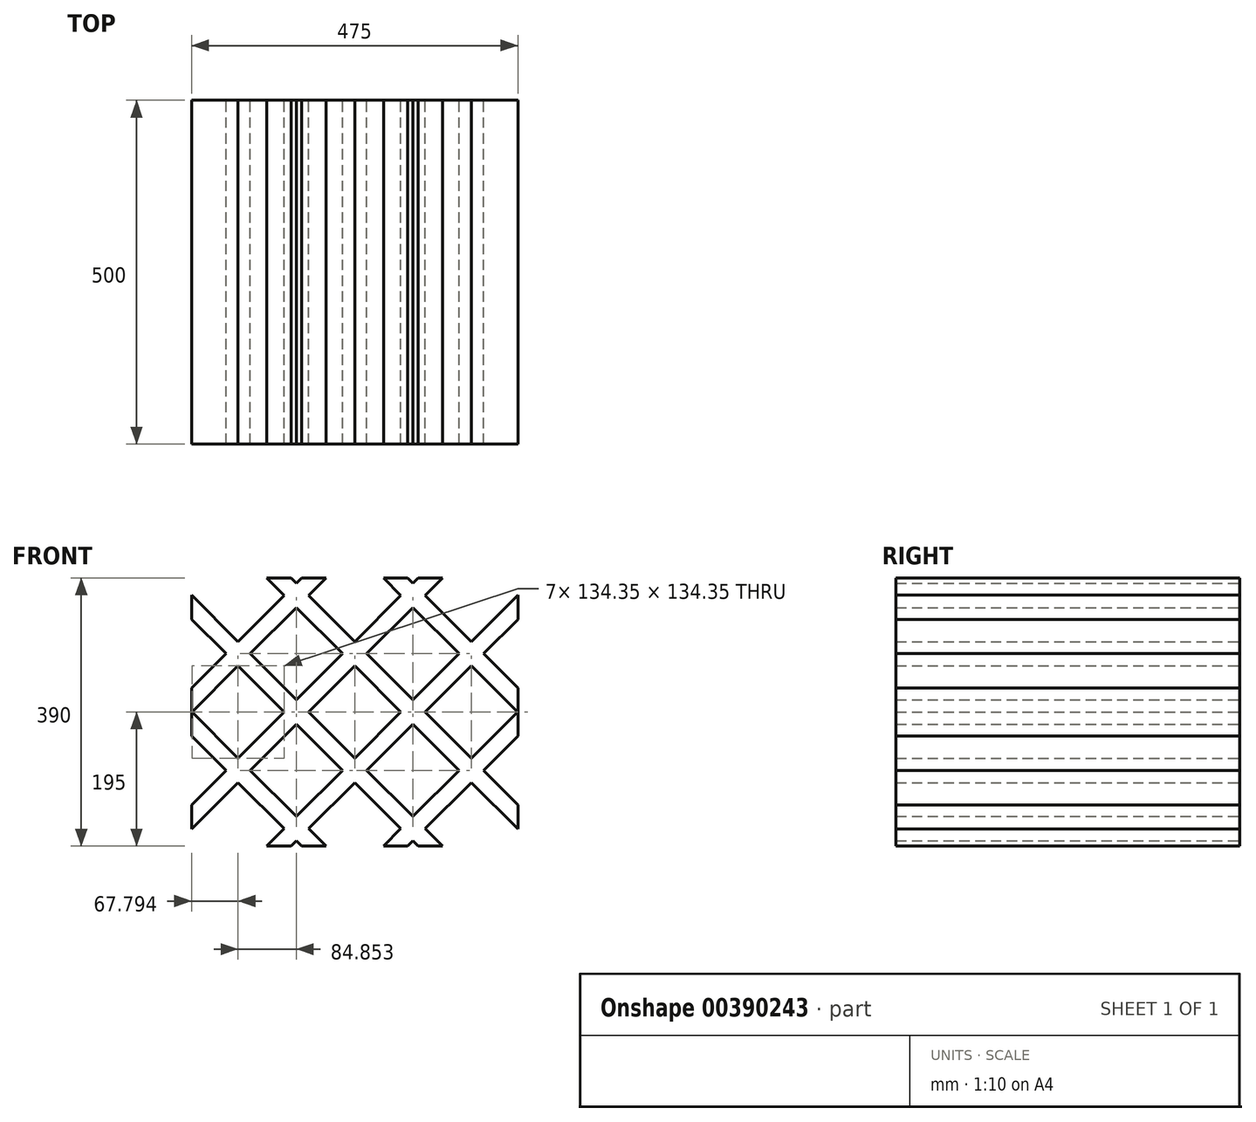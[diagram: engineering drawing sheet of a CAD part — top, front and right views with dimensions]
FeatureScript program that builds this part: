
annotation { "Feature Type Name" : "Feature", "Feature Type Description" : "" }
export const myFeature = defineFeature(function(context is Context, id is Id, definition is map)
    precondition{}
    {
        {
            var Q0;
            Q0=qCreatedBy(makeId("Front.planeOp"),FACE);
            var sketch = newSketch(context, id + "F0", { "sketchPlane" : qUnion([Q0])});
            skLineSegment(sketch, "E0.bottom", {"start": v(237.5, -195) * mm, "end": v(-237.5, -195) * mm, "construction": true});
            skLineSegment(sketch, "E0.top", {"start": v(237.5, 195) * mm, "end": v(-237.5, 195) * mm, "construction": true});
            skLineSegment(sketch, "E0.left", {"start": v(237.5, -195) * mm, "end": v(237.5, 195) * mm, "construction": true});
            skLineSegment(sketch, "E0.right", {"start": v(-237.5, -195) * mm, "end": v(-237.5, 195) * mm, "construction": true});
            skPoint(sketch, "E0.middle", {"position": v(0, 0) * mm});
            skLineSegment(sketch, "E1", {"start": v(-237.5, 152.65) * mm, "end": v(110.15, -195) * mm, "construction": true});
            skLineSegment(sketch, "E2", {"start": v(-110.15, 195) * mm, "end": v(237.5, -152.65) * mm, "construction": true});
            skLineSegment(sketch, "E3", {"start": v(59.56, 195) * mm, "end": v(237.5, 17.06) * mm, "construction": true});
            skLineSegment(sketch, "E4", {"start": v(-237.5, -17.06) * mm, "end": v(-59.56, -195) * mm, "construction": true});
            skLineSegment(sketch, "E5", {"start": v(110.15, 195) * mm, "end": v(-237.5, -152.65) * mm, "construction": true});
            skLineSegment(sketch, "E6", {"start": v(237.5, 152.65) * mm, "end": v(-110.15, -195) * mm, "construction": true});
            skLineSegment(sketch, "E7", {"start": v(-59.56, 195) * mm, "end": v(-237.5, 17.06) * mm, "construction": true});
            skLineSegment(sketch, "E8", {"start": v(237.5, -17.06) * mm, "end": v(59.56, -195) * mm, "construction": true});
            skLineSegment(sketch, "E9", {"start": v(237.5, 34.74) * mm, "end": v(237.5, -0.62) * mm});
            skLineSegment(sketch, "E10", {"start": v(237.5, 0.62) * mm, "end": v(237.5, -34.74) * mm});
            skLineSegment(sketch, "E11", {"start": v(237.5, -134.97) * mm, "end": v(237.5, -170.32) * mm});
            skLineSegment(sketch, "E12", {"start": v(-127.82, 195) * mm, "end": v(-102.53, 169.7) * mm});
            skLineSegment(sketch, "E13", {"start": v(-102.53, 169.7) * mm, "end": v(-169.7, 102.53) * mm});
            skLineSegment(sketch, "E14", {"start": v(-237.5, 170.32) * mm, "end": v(-169.7, 102.53) * mm});
            skLineSegment(sketch, "E15", {"start": v(-237.5, 170.32) * mm, "end": v(-237.5, 134.97) * mm});
            skLineSegment(sketch, "E16", {"start": v(-237.5, 134.97) * mm, "end": v(-187.38, 84.85) * mm});
            skLineSegment(sketch, "E17", {"start": v(-187.38, 84.85) * mm, "end": v(-237.5, 34.74) * mm});
            skLineSegment(sketch, "E18", {"start": v(-237.5, 34.74) * mm, "end": v(-237.5, -0.62) * mm});
            skLineSegment(sketch, "E19", {"start": v(-237.5, -0.62) * mm, "end": v(-169.7, 67.18) * mm});
            skLineSegment(sketch, "E20", {"start": v(-169.7, 67.18) * mm, "end": v(-102.53, 0) * mm});
            skLineSegment(sketch, "E21", {"start": v(-102.53, 0) * mm, "end": v(-169.7, -67.18) * mm});
            skLineSegment(sketch, "E22", {"start": v(-169.7, -67.18) * mm, "end": v(-237.5, 0.62) * mm});
            skLineSegment(sketch, "E23", {"start": v(-237.5, 0.62) * mm, "end": v(-237.5, -34.74) * mm});
            skLineSegment(sketch, "E24", {"start": v(-237.5, -34.74) * mm, "end": v(-187.38, -84.85) * mm});
            skLineSegment(sketch, "E25", {"start": v(-187.38, -84.85) * mm, "end": v(-237.5, -134.97) * mm});
            skLineSegment(sketch, "E26", {"start": v(-237.5, -134.97) * mm, "end": v(-237.5, -170.32) * mm});
            skLineSegment(sketch, "E27", {"start": v(-237.5, -170.32) * mm, "end": v(-169.7, -102.53) * mm});
            skLineSegment(sketch, "E28", {"start": v(-169.7, -102.53) * mm, "end": v(-102.53, -169.7) * mm});
            skLineSegment(sketch, "E29", {"start": v(-102.53, -169.7) * mm, "end": v(-127.82, -195) * mm});
            skLineSegment(sketch, "E30", {"start": v(-127.82, -195) * mm, "end": v(-92.47, -195) * mm});
            skLineSegment(sketch, "E31", {"start": v(-92.47, -195) * mm, "end": v(-84.85, -187.38) * mm});
            skLineSegment(sketch, "E32", {"start": v(-84.85, -187.38) * mm, "end": v(-77.24, -195) * mm});
            skLineSegment(sketch, "E33", {"start": v(-77.24, -195) * mm, "end": v(-41.88, -195) * mm});
            skLineSegment(sketch, "E34", {"start": v(-41.88, -195) * mm, "end": v(-67.18, -169.7) * mm});
            skLineSegment(sketch, "E35", {"start": v(-67.18, -169.7) * mm, "end": v(0, -102.53) * mm});
            skLineSegment(sketch, "E36", {"start": v(0, -102.53) * mm, "end": v(67.18, -169.7) * mm});
            skLineSegment(sketch, "E37", {"start": v(67.18, -169.7) * mm, "end": v(41.88, -195) * mm});
            skLineSegment(sketch, "E38", {"start": v(41.88, -195) * mm, "end": v(77.24, -195) * mm});
            skLineSegment(sketch, "E39", {"start": v(77.24, -195) * mm, "end": v(84.85, -187.38) * mm});
            skLineSegment(sketch, "E40", {"start": v(84.85, -187.38) * mm, "end": v(92.47, -195) * mm});
            skLineSegment(sketch, "E41", {"start": v(92.47, -195) * mm, "end": v(127.82, -195) * mm});
            skLineSegment(sketch, "E42", {"start": v(127.82, -195) * mm, "end": v(102.53, -169.7) * mm});
            skLineSegment(sketch, "E43", {"start": v(102.53, -169.7) * mm, "end": v(169.7, -102.53) * mm});
            skLineSegment(sketch, "E44", {"start": v(169.7, -102.53) * mm, "end": v(237.5, -170.32) * mm});
            skLineSegment(sketch, "E45", {"start": v(237.5, -134.97) * mm, "end": v(187.38, -84.85) * mm});
            skLineSegment(sketch, "E46", {"start": v(187.38, -84.85) * mm, "end": v(237.5, -34.74) * mm});
            skLineSegment(sketch, "E47", {"start": v(237.5, 0.62) * mm, "end": v(169.7, -67.18) * mm});
            skLineSegment(sketch, "E48", {"start": v(169.7, -67.18) * mm, "end": v(102.53, 0) * mm});
            skLineSegment(sketch, "E49", {"start": v(102.53, 0) * mm, "end": v(169.7, 67.18) * mm});
            skLineSegment(sketch, "E50", {"start": v(169.7, 67.18) * mm, "end": v(237.5, -0.62) * mm});
            skLineSegment(sketch, "E51", {"start": v(237.5, 34.74) * mm, "end": v(187.38, 84.85) * mm});
            skLineSegment(sketch, "E52", {"start": v(187.38, 84.85) * mm, "end": v(237.5, 134.97) * mm});
            skLineSegment(sketch, "E53", {"start": v(237.5, 134.97) * mm, "end": v(237.5, 170.32) * mm});
            skLineSegment(sketch, "E54", {"start": v(237.5, 170.32) * mm, "end": v(169.7, 102.53) * mm});
            skLineSegment(sketch, "E55", {"start": v(169.7, 102.53) * mm, "end": v(102.53, 169.7) * mm});
            skLineSegment(sketch, "E56", {"start": v(102.53, 169.7) * mm, "end": v(127.82, 195) * mm});
            skLineSegment(sketch, "E57", {"start": v(127.82, 195) * mm, "end": v(92.47, 195) * mm});
            skLineSegment(sketch, "E58", {"start": v(77.24, 195) * mm, "end": v(41.88, 195) * mm});
            skLineSegment(sketch, "E59", {"start": v(41.88, 195) * mm, "end": v(67.18, 169.7) * mm});
            skLineSegment(sketch, "E60", {"start": v(67.18, 169.7) * mm, "end": v(0, 102.53) * mm});
            skLineSegment(sketch, "E61", {"start": v(0, 102.53) * mm, "end": v(-67.18, 169.7) * mm});
            skLineSegment(sketch, "E62", {"start": v(-67.18, 169.7) * mm, "end": v(-41.88, 195) * mm});
            skLineSegment(sketch, "E63", {"start": v(-41.88, 195) * mm, "end": v(-77.24, 195) * mm});
            skLineSegment(sketch, "E64", {"start": v(-127.82, 195) * mm, "end": v(-92.47, 195) * mm});
            skLineSegment(sketch, "E65", {"start": v(-92.47, 195) * mm, "end": v(-84.85, 187.38) * mm});
            skLineSegment(sketch, "E66", {"start": v(-84.85, 187.38) * mm, "end": v(-77.24, 195) * mm});
            skLineSegment(sketch, "E67", {"start": v(77.24, 195) * mm, "end": v(84.85, 187.38) * mm});
            skLineSegment(sketch, "E68", {"start": v(84.85, 187.38) * mm, "end": v(92.47, 195) * mm});
            skLineSegment(sketch, "E69.bottom", {"start": v(-84.85, 17.68) * mm, "end": v(-152.03, 84.85) * mm});
            skLineSegment(sketch, "E69.top", {"start": v(-17.68, 84.85) * mm, "end": v(-84.85, 152.03) * mm});
            skLineSegment(sketch, "E69.left", {"start": v(-84.85, 17.68) * mm, "end": v(-17.68, 84.85) * mm});
            skLineSegment(sketch, "E69.right", {"start": v(-152.03, 84.85) * mm, "end": v(-84.85, 152.03) * mm});
            skPoint(sketch, "E69.middle", {"position": v(-84.85, 84.85) * mm});
            skLineSegment(sketch, "E70.bottom", {"start": v(0, -67.18) * mm, "end": v(-67.18, 0) * mm});
            skLineSegment(sketch, "E70.top", {"start": v(67.18, 0) * mm, "end": v(0, 67.18) * mm});
            skLineSegment(sketch, "E70.left", {"start": v(0, -67.18) * mm, "end": v(67.18, 0) * mm});
            skLineSegment(sketch, "E70.right", {"start": v(-67.18, 0) * mm, "end": v(0, 67.18) * mm});
            skLineSegment(sketch, "E71.bottom", {"start": v(84.85, 17.68) * mm, "end": v(17.68, 84.85) * mm});
            skLineSegment(sketch, "E71.top", {"start": v(152.03, 84.85) * mm, "end": v(84.85, 152.03) * mm});
            skLineSegment(sketch, "E71.left", {"start": v(84.85, 17.68) * mm, "end": v(152.03, 84.85) * mm});
            skLineSegment(sketch, "E71.right", {"start": v(17.68, 84.85) * mm, "end": v(84.85, 152.03) * mm});
            skPoint(sketch, "E71.middle", {"position": v(84.85, 84.85) * mm});
            skLineSegment(sketch, "E72.bottom", {"start": v(84.85, -152.03) * mm, "end": v(17.68, -84.85) * mm});
            skLineSegment(sketch, "E72.top", {"start": v(152.03, -84.85) * mm, "end": v(84.85, -17.68) * mm});
            skLineSegment(sketch, "E72.left", {"start": v(84.85, -152.03) * mm, "end": v(152.03, -84.85) * mm});
            skLineSegment(sketch, "E72.right", {"start": v(17.68, -84.85) * mm, "end": v(84.85, -17.68) * mm});
            skPoint(sketch, "E72.middle", {"position": v(84.85, -84.85) * mm});
            skLineSegment(sketch, "E73.bottom", {"start": v(-84.85, -152.03) * mm, "end": v(-152.03, -84.85) * mm});
            skLineSegment(sketch, "E73.top", {"start": v(-17.68, -84.85) * mm, "end": v(-84.85, -17.68) * mm});
            skLineSegment(sketch, "E73.left", {"start": v(-84.85, -152.03) * mm, "end": v(-17.68, -84.85) * mm});
            skLineSegment(sketch, "E73.right", {"start": v(-152.03, -84.85) * mm, "end": v(-84.85, -17.68) * mm});
            skPoint(sketch, "E73.middle", {"position": v(-84.85, -84.85) * mm});
            skSolve(sketch);
        }
        {
            var Q0;
            Q0 = qSketchRegion(id + "F0", true);
            extrude(context, id + "F1", {"entities" : qUnion([Q0]), "depth" : 500 * mm});
        }
    });
